# Revit family: 207_Uteluftkappe _ 00788
name_source: partatom
category: Air Terminals
revit_build: Autodesk Revit 2018 (Build: 20170223_1515(x64)
units: mm (PartAtom-declared; Revit-internal decimal feet)

## family parameters
Always vertical = Yes
Cut with Voids When Loaded = No
Part Type = Normal
Room Calculation Point = Yes
Round Connector Dimension = Use Diameter
Shared = No
Work Plane-Based = No

## types (1)
- 160-00788
    CAT0 = Yes
    CLBTZ = 0 mm  [stored 0 ft]
    CL_Location_5000 = 5000 mm  [stored 16.4042 ft]
    D = 160 mm
    Description = Air cowl exhaust/outdoor  male
    H_ARR = 0 mm  [stored 0 ft]
    L_ARR = 400 mm  [stored 1.31234 ft]
    MC Product Code = 160-00788
    Manufacturer = Flexit
    QmdConnectorList = 201;D
    W_ARR = 400 mm  [stored 1.31234 ft]
    X2 = 5 mm  [stored 0.0164042 ft]
    X3 = 100 mm  [stored 0.328084 ft]
    X4 = 25 mm  [stored 0.082021 ft]
    XRefLineVPlnId = 7453
    Y1 = 121 mm
    Y2 = 10 mm  [stored 0.0328084 ft]
    Y3 = 221 mm  [stored 0.725066 ft]
    YRefLineVPlnId = 7456
    Z1 = 117 mm
    Z2 = 16 mm  [stored 0.0524934 ft]
    Z3 = 20 mm  [stored 0.0656168 ft]
    Z4 = 40 mm  [stored 0.131234 ft]
    magiPartTypeId = 207
    magiProductFamilyId = Uteluftkappe * 00788
    magiProductId = Uteluftkappe 160

note: [stored X ft] marks values corroborated as IEEE doubles in the binary element streams (Revit-internal decimal feet)

## geometry (parser evidence)
native form markers: Sweep x2
no freeform markers — native parametric forms only
